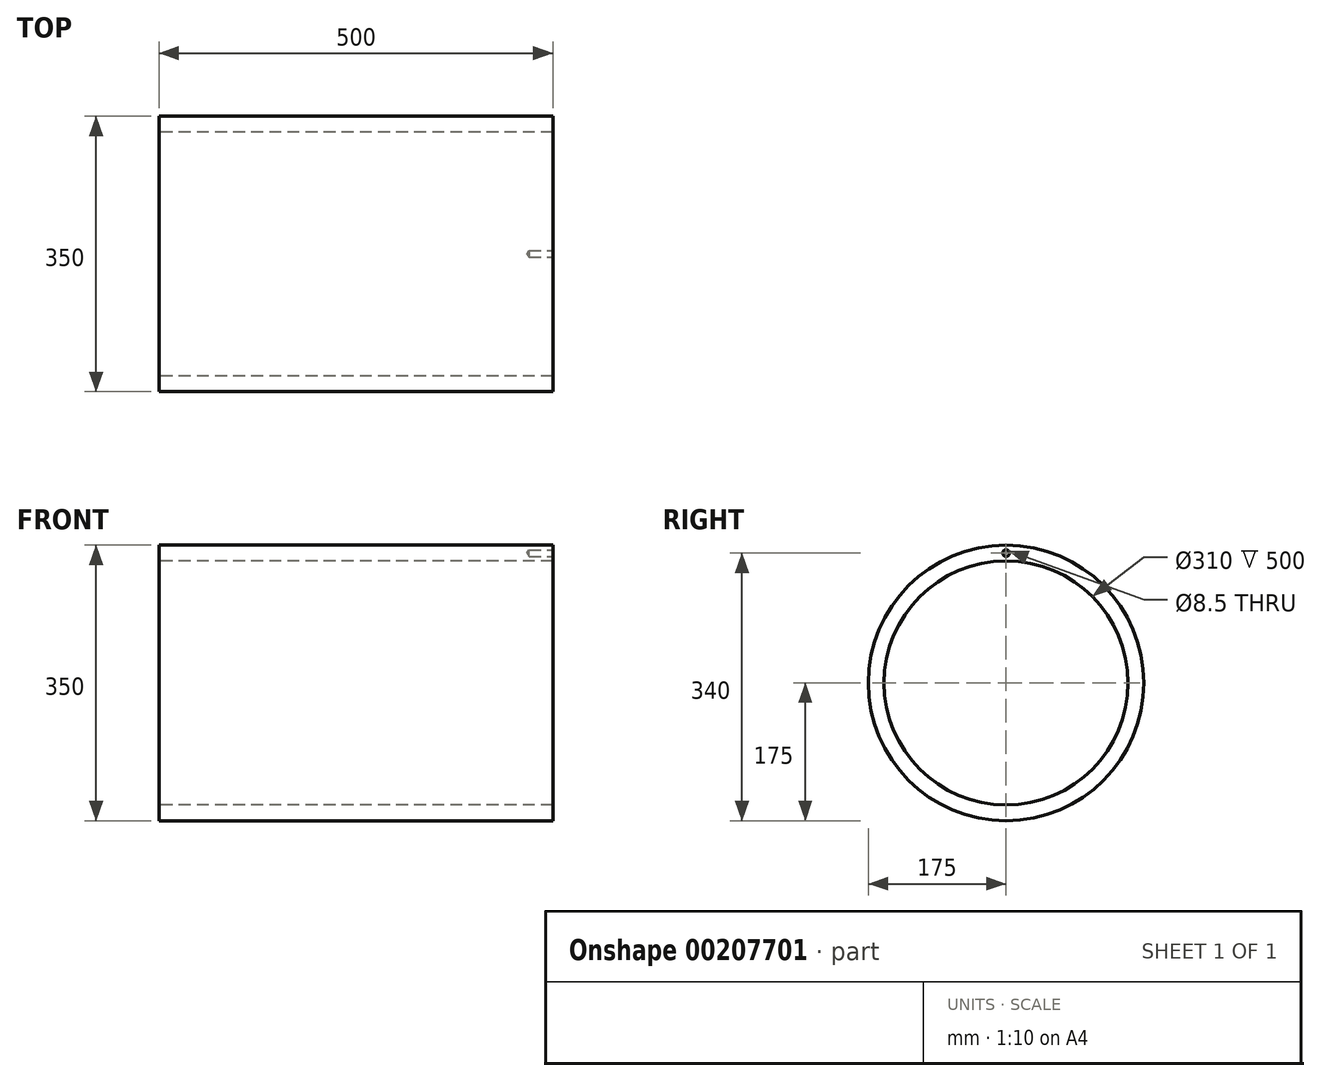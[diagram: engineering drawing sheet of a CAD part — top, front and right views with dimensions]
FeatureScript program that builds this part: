
annotation { "Feature Type Name" : "Feature", "Feature Type Description" : "" }
export const myFeature = defineFeature(function(context is Context, id is Id, definition is map)
    precondition{}
    {
        {
            var Q0;
            Q0=qCreatedBy(makeId("Front.planeOp"),FACE);
            var sketch = newSketch(context, id + "F0", { "sketchPlane" : qUnion([Q0])});
            skLineSegment(sketch, "E0", {"start": v(-250, 175) * mm, "end": v(-250, 155) * mm});
            skLineSegment(sketch, "E1", {"start": v(-250, 155) * mm, "end": v(0, 155) * mm});
            skLineSegment(sketch, "E2", {"start": v(0, 226.66) * mm, "end": v(0, 155) * mm, "construction": true});
            skLineSegment(sketch, "E3", {"start": v(-250, 0) * mm, "end": v(0, 0) * mm, "construction": true});
            skLineSegment(sketch, "E4.MirrorCS", {"start": v(250, 175) * mm, "end": v(250, 155) * mm});
            skLineSegment(sketch, "E5.MirrorCS", {"start": v(250, 155) * mm, "end": v(0, 155) * mm});
            skLineSegment(sketch, "E6", {"start": v(250, 175) * mm, "end": v(-250, 175) * mm});
            skSolve(sketch);
        }
        {
            var Q0;
            Q0=makeQuery(id+"F0.imprint","IMPRINT",FACE,{"disambiguationData":[TD([[makeQuery(id+"F0.imprint","IMPRINT",EDGE,{"derivedFrom":sQuery(id+"F0.wireOp",EDGE,"E0")}),1.0]])]});
            var Q1;
            Q1=sQuery(id+"F0.wireOp",EDGE,"E3");
            revolve(context, id + "F1", {"entities" : qUnion([Q0]), "axis" : qUnion([Q1]), "revolveType" : RevolveType.FULL});
        }
        {
            var Q0;
            Q0=makeQuery(id+"F1.opRevolve","SWEPT_FACE",FACE,{"disambiguationData":[OSD([sQuery(id+"F0.wireOp",EDGE,"E4.MirrorCS")])]});
            var sketch = newSketch(context, id + "F2", { "sketchPlane" : qUnion([Q0])});
            skCircle(sketch, "E7", {"center": v(0, 165) * mm, "radius": 5 * mm});
            skSolve(sketch);
        }
        {
            var Q0;
            Q0=sQuery(id+"F2.wireOp",VERTEX,"E7.center");
            var Q1;
            Q1=makeQuery(id+"F1.opRevolve","SWEPT_BODY",BODY,{"disambiguationData":[OSD([sQuery(id+"F0.wireOp",EDGE,"E0"),sQuery(id+"F0.wireOp",EDGE,"E1"),sQuery(id+"F0.wireOp",EDGE,"E4.MirrorCS"),sQuery(id+"F0.wireOp",EDGE,"E5.MirrorCS"),sQuery(id+"F0.wireOp",EDGE,"E6")])]});
            hole(context, id + "F3", {"style" : HoleStyle.SIMPLE, "endStyle" : HoleEndStyle.BLIND, "standardTappedOrClearance" : lookupTablePath({ "standard" : "ISO", "engagement" : "75%", "pitch" : "1.5 mm", "size" : "M10", "type" : "Tapped" }), "standardBlindInLast" : lookupTablePath({ "standard" : "ISO", "engagement" : "75%", "pitch" : "1.5 mm", "size" : "M10", "type" : "Tapped" }), "holeDiameter" : 8.5 * mm, "showTappedDepth" : true, "holeDepth" : 30 * mm, "tappedDepth" : 25.5 * mm, "tapClearance" : 3, "locations" : qUnion([Q0]), "scope" : qUnion([Q1]), "majorDiameter" : 10 * mm});
        }
    });
